# Revit family: Casement_34_D_Top_Hung_Standard
name_source: partatom
category: Windows
revit_build: Autodesk Revit 2014 (Build: 20130308_1515(x64)
units: mm (PartAtom-declared; Revit-internal decimal feet)

## types (12) — shared parameters
Aluminium Thickness = 1 mm  [stored 0.00328084 ft]
Bead SG Gap = 13 mm  [stored 0.0426509 ft]
Bottom Hung = No
Casement Dimension = 34 mm  [stored 0.111549 ft]
Custom Sash Height = 554 mm  [stored 1.81759 ft]
DG Extrusion Start = 7 mm  [stored 0.0229659 ft]
DG Gasket Finish = Double Glazing Gasket Material
DG Thickness Calc = 4 mm  [stored 0.0131234 ft]
Default Sill Height = 800 mm  [stored 2.62467 ft]
Depth Bead = 20 mm  [stored 0.0656168 ft]
Description = Window 34mm, Type D top hung
Frame Center Offset = 17 mm
Height Panel 1 = 540 mm  [stored 1.77165 ft]
Height Sash = 524 mm  [stored 1.71916 ft]
Height Sash Opening = 554 mm  [stored 1.81759 ft]
Limit Fixed Pane Height Max = 1800 mm  [stored 5.90551 ft]
Limit Fixed Pane Height Min = 200 mm  [stored 0.656168 ft]
Limit Sash Height Max = 900 mm  [stored 2.95276 ft]
Limit Sash Height Min = 300 mm  [stored 0.984252 ft]
Limit Sash Width Max = 1200 mm
Limit Sash Width Min = 300 mm  [stored 0.984252 ft]
Limit Window Height Max = 2430 mm
Limit Window Height Min = 830 mm  [stored 2.7231 ft]
Limit Window Width Max = 1246 mm  [stored 4.08793 ft]
Limit Window Width Min = 346 mm
Manufacturer = Crealco
Max System DG One Piece Thickness = 4 mm  [stored 0.0131234 ft]
Max System DG Unit Thickness = 20 mm  [stored 0.0656168 ft]
Model = Casement 34
Offset Bead SG Center Reversed = 17 mm
Offset Panel 3 Bead Top = 600 mm  [stored 1.9685 ft]
Offset Sash Left = 23 mm  [stored 0.0754593 ft]
Offset Sash Top = 23 mm  [stored 0.0754593 ft]
Offset Transom Top = 570 mm  [stored 1.87008 ft]
Offset Window Exterior = 17 mm
SG Gasket Thickness = 6 mm  [stored 0.019685 ft]
Sash Center Offset = 14 mm  [stored 0.0459318 ft]
Sash Overlap = 7 mm  [stored 0.0229659 ft]
Sash Spacing Inner = 8 mm  [stored 0.0262467 ft]
Top Hung = Yes
URL = http://www.crealco.co.za
Wall Closure = By host
Width Bead = 15 mm  [stored 0.0492126 ft]
Width Profile = 30 mm  [stored 0.0984252 ft]
zero-valued in all types: Window Exterior Offset

## per-type parameters (varying)
- 34-0609T-1000Pa: Area Pane Bottom=0.13 m²; Area Pane Top=0.23 m²; Clearvue Insulated LowE SHGC Value=0.43; Clearvue Insulated LowE U Value=3.94; Clearvue Insulated SHGC Value=0.471; Clearvue Insulated U Value=4.36; Clearvue SHGC Value=0.529; Clearvue U Value=6.18; Custom Windload=1000 mm  [stored 3.28084 ft]; Custom Window Height=890 mm  [stored 2.91995 ft]; Custom Window Width=590 mm  [stored 1.9357 ft]; Energy Advantage SHGC Value=0.475; Energy Advantage U Value=4.96; Height=890 mm  [stored 2.91995 ft]; Height Panel 3=260 mm; Intruderprufe LowE SHGC Value=0.446; Intruderprufe LowE U Value=4.84; Intruderprufe SHGC Value=0.499; Intruderprufe U Value=6.13; Length Transom=530 mm  [stored 1.73885 ft]; Max Pane Area=0.23 m²; Width=590 mm  [stored 1.9357 ft]; Width Panel 1=530 mm  [stored 1.73885 ft]; Width Panel 3=530 mm  [stored 1.73885 ft]; Width Sash=514 mm; Width Sash Opening=544 mm  [stored 1.78478 ft]; Windload Design=1000 mm  [stored 3.28084 ft]
- 34-0609T-1500Pa: Area Pane Bottom=0.13 m²; Area Pane Top=0.23 m²; Clearvue Insulated LowE SHGC Value=0.43; Clearvue Insulated LowE U Value=3.94; Clearvue Insulated SHGC Value=0.471; Clearvue Insulated U Value=4.36; Clearvue SHGC Value=0.529; Clearvue U Value=6.18; Custom Windload=1500 mm  [stored 4.92126 ft]; Custom Window Height=890 mm  [stored 2.91995 ft]; Custom Window Width=590 mm  [stored 1.9357 ft]; Energy Advantage SHGC Value=0.475; Energy Advantage U Value=4.96; Height=890 mm  [stored 2.91995 ft]; Height Panel 3=260 mm; Intruderprufe LowE SHGC Value=0.446; Intruderprufe LowE U Value=4.84; Intruderprufe SHGC Value=0.499; Intruderprufe U Value=6.13; Length Transom=530 mm  [stored 1.73885 ft]; Max Pane Area=0.23 m²; Width=590 mm  [stored 1.9357 ft]; Width Panel 1=530 mm  [stored 1.73885 ft]; Width Panel 3=530 mm  [stored 1.73885 ft]; Width Sash=514 mm; Width Sash Opening=544 mm  [stored 1.78478 ft]; Windload Design=1500 mm  [stored 4.92126 ft]
- 34-0609T-2000Pa: Area Pane Bottom=0.13 m²; Area Pane Top=0.23 m²; Clearvue Insulated LowE SHGC Value=0.43; Clearvue Insulated LowE U Value=3.94; Clearvue Insulated SHGC Value=0.471; Clearvue Insulated U Value=4.36; Clearvue SHGC Value=0.529; Clearvue U Value=6.18; Custom Windload=2000 mm; Custom Window Height=890 mm  [stored 2.91995 ft]; Custom Window Width=590 mm  [stored 1.9357 ft]; Energy Advantage SHGC Value=0.475; Energy Advantage U Value=4.96; Height=890 mm  [stored 2.91995 ft]; Height Panel 3=260 mm; Intruderprufe LowE SHGC Value=0.446; Intruderprufe LowE U Value=4.84; Intruderprufe SHGC Value=0.499; Intruderprufe U Value=6.13; Length Transom=530 mm  [stored 1.73885 ft]; Max Pane Area=0.23 m²; Width=590 mm  [stored 1.9357 ft]; Width Panel 1=530 mm  [stored 1.73885 ft]; Width Panel 3=530 mm  [stored 1.73885 ft]; Width Sash=514 mm; Width Sash Opening=544 mm  [stored 1.78478 ft]; Windload Design=2000 mm
- 34-0909T-1000Pa: Area Pane Bottom=0.21 m²; Area Pane Top=0.37 m²; Clearvue Insulated LowE SHGC Value=0.465; Clearvue Insulated LowE U Value=3.68; Clearvue Insulated SHGC Value=0.51; Clearvue Insulated U Value=4.15; Clearvue SHGC Value=0.574; Clearvue U Value=6.15; Custom Windload=1000 mm  [stored 3.28084 ft]; Custom Window Height=890 mm  [stored 2.91995 ft]; Custom Window Width=890 mm  [stored 2.91995 ft]; Energy Advantage SHGC Value=0.514; Energy Advantage U Value=4.79; Height=890 mm  [stored 2.91995 ft]; Height Panel 3=260 mm; Intruderprufe LowE SHGC Value=0.483; Intruderprufe LowE U Value=4.68; Intruderprufe SHGC Value=0.542; Intruderprufe U Value=6.1; Length Transom=830 mm  [stored 2.7231 ft]; Max Pane Area=0.37 m²; Width=890 mm  [stored 2.91995 ft]; Width Panel 1=830 mm  [stored 2.7231 ft]; Width Panel 3=830 mm  [stored 2.7231 ft]; Width Sash=814 mm  [stored 2.6706 ft]; Width Sash Opening=844 mm  [stored 2.76903 ft]; Windload Design=1000 mm  [stored 3.28084 ft]
- 34-0909T-1500Pa: Area Pane Bottom=0.21 m²; Area Pane Top=0.37 m²; Clearvue Insulated LowE SHGC Value=0.465; Clearvue Insulated LowE U Value=3.68; Clearvue Insulated SHGC Value=0.51; Clearvue Insulated U Value=4.15; Clearvue SHGC Value=0.574; Clearvue U Value=6.15; Custom Windload=1500 mm  [stored 4.92126 ft]; Custom Window Height=890 mm  [stored 2.91995 ft]; Custom Window Width=890 mm  [stored 2.91995 ft]; Energy Advantage SHGC Value=0.514; Energy Advantage U Value=4.79; Height=890 mm  [stored 2.91995 ft]; Height Panel 3=260 mm; Intruderprufe LowE SHGC Value=0.483; Intruderprufe LowE U Value=4.68; Intruderprufe SHGC Value=0.542; Intruderprufe U Value=6.1; Length Transom=830 mm  [stored 2.7231 ft]; Max Pane Area=0.37 m²; Width=890 mm  [stored 2.91995 ft]; Width Panel 1=830 mm  [stored 2.7231 ft]; Width Panel 3=830 mm  [stored 2.7231 ft]; Width Sash=814 mm  [stored 2.6706 ft]; Width Sash Opening=844 mm  [stored 2.76903 ft]; Windload Design=1500 mm  [stored 4.92126 ft]
- 34-0909T-2000Pa: Area Pane Bottom=0.21 m²; Area Pane Top=0.37 m²; Clearvue Insulated LowE SHGC Value=0.465; Clearvue Insulated LowE U Value=3.68; Clearvue Insulated SHGC Value=0.51; Clearvue Insulated U Value=4.15; Clearvue SHGC Value=0.574; Clearvue U Value=6.15; Custom Windload=2000 mm; Custom Window Height=890 mm  [stored 2.91995 ft]; Custom Window Width=890 mm  [stored 2.91995 ft]; Energy Advantage SHGC Value=0.514; Energy Advantage U Value=4.79; Height=890 mm  [stored 2.91995 ft]; Height Panel 3=260 mm; Intruderprufe LowE SHGC Value=0.483; Intruderprufe LowE U Value=4.68; Intruderprufe SHGC Value=0.542; Intruderprufe U Value=6.1; Length Transom=830 mm  [stored 2.7231 ft]; Max Pane Area=0.37 m²; Width=890 mm  [stored 2.91995 ft]; Width Panel 1=830 mm  [stored 2.7231 ft]; Width Panel 3=830 mm  [stored 2.7231 ft]; Width Sash=814 mm  [stored 2.6706 ft]; Width Sash Opening=844 mm  [stored 2.76903 ft]; Windload Design=2000 mm
- 34-0612T-1000Pa: Area Pane Bottom=0.29 m²; Area Pane Top=0.23 m²; Clearvue Insulated LowE SHGC Value=0.467; Clearvue Insulated LowE U Value=3.65; Clearvue Insulated SHGC Value=0.513; Clearvue Insulated U Value=4.12; Clearvue SHGC Value=0.576; Clearvue U Value=6.13; Custom Windload=1000 mm  [stored 3.28084 ft]; Custom Window Height=1190 mm  [stored 3.9042 ft]; Custom Window Width=590 mm  [stored 1.9357 ft]; Energy Advantage SHGC Value=0.516; Energy Advantage U Value=4.77; Height=1190 mm  [stored 3.9042 ft]; Height Panel 3=560 mm; Intruderprufe LowE SHGC Value=0.485; Intruderprufe LowE U Value=4.66; Intruderprufe SHGC Value=0.544; Intruderprufe U Value=6.06; Length Transom=530 mm  [stored 1.73885 ft]; Max Pane Area=0.29 m²; Width=590 mm  [stored 1.9357 ft]; Width Panel 1=530 mm  [stored 1.73885 ft]; Width Panel 3=530 mm  [stored 1.73885 ft]; Width Sash=514 mm; Width Sash Opening=544 mm  [stored 1.78478 ft]; Windload Design=1000 mm  [stored 3.28084 ft]
- 34-0612T-1500Pa: Area Pane Bottom=0.29 m²; Area Pane Top=0.23 m²; Clearvue Insulated LowE SHGC Value=0.467; Clearvue Insulated LowE U Value=3.65; Clearvue Insulated SHGC Value=0.513; Clearvue Insulated U Value=4.12; Clearvue SHGC Value=0.576; Clearvue U Value=6.13; Custom Windload=1500 mm  [stored 4.92126 ft]; Custom Window Height=1190 mm  [stored 3.9042 ft]; Custom Window Width=590 mm  [stored 1.9357 ft]; Energy Advantage SHGC Value=0.516; Energy Advantage U Value=4.77; Height=1190 mm  [stored 3.9042 ft]; Height Panel 3=560 mm; Intruderprufe LowE SHGC Value=0.485; Intruderprufe LowE U Value=4.66; Intruderprufe SHGC Value=0.544; Intruderprufe U Value=6.06; Length Transom=530 mm  [stored 1.73885 ft]; Max Pane Area=0.29 m²; Width=590 mm  [stored 1.9357 ft]; Width Panel 1=530 mm  [stored 1.73885 ft]; Width Panel 3=530 mm  [stored 1.73885 ft]; Width Sash=514 mm; Width Sash Opening=544 mm  [stored 1.78478 ft]; Windload Design=1500 mm  [stored 4.92126 ft]
- 34-0612T-2000Pa: Area Pane Bottom=0.29 m²; Area Pane Top=0.23 m²; Clearvue Insulated LowE SHGC Value=0.467; Clearvue Insulated LowE U Value=3.65; Clearvue Insulated SHGC Value=0.513; Clearvue Insulated U Value=4.12; Clearvue SHGC Value=0.576; Clearvue U Value=6.13; Custom Windload=2000 mm; Custom Window Height=1190 mm  [stored 3.9042 ft]; Custom Window Width=590 mm  [stored 1.9357 ft]; Energy Advantage SHGC Value=0.516; Energy Advantage U Value=4.77; Height=1190 mm  [stored 3.9042 ft]; Height Panel 3=560 mm; Intruderprufe LowE SHGC Value=0.485; Intruderprufe LowE U Value=4.66; Intruderprufe SHGC Value=0.544; Intruderprufe U Value=6.06; Length Transom=530 mm  [stored 1.73885 ft]; Max Pane Area=0.29 m²; Width=590 mm  [stored 1.9357 ft]; Width Panel 1=530 mm  [stored 1.73885 ft]; Width Panel 3=530 mm  [stored 1.73885 ft]; Width Sash=514 mm; Width Sash Opening=544 mm  [stored 1.78478 ft]; Windload Design=2000 mm
- 34-0912T-1000Pa: Area Pane Bottom=0.45 m²; Area Pane Top=0.37 m²; Clearvue Insulated LowE SHGC Value=0.502; Clearvue Insulated LowE U Value=3.38; Clearvue Insulated SHGC Value=0.552; Clearvue Insulated U Value=3.91; Clearvue SHGC Value=0.621; Clearvue U Value=6.1; Custom Windload=1000 mm  [stored 3.28084 ft]; Custom Window Height=1190 mm  [stored 3.9042 ft]; Custom Window Width=890 mm  [stored 2.91995 ft]; Energy Advantage SHGC Value=0.556; Energy Advantage U Value=4.6; Height=1190 mm  [stored 3.9042 ft]; Height Panel 3=560 mm; Intruderprufe LowE SHGC Value=0.521; Intruderprufe LowE U Value=4.49; Intruderprufe SHGC Value=0.587; Intruderprufe U Value=6.02; Length Transom=830 mm  [stored 2.7231 ft]; Max Pane Area=0.45 m²; Width=890 mm  [stored 2.91995 ft]; Width Panel 1=830 mm  [stored 2.7231 ft]; Width Panel 3=830 mm  [stored 2.7231 ft]; Width Sash=814 mm  [stored 2.6706 ft]; Width Sash Opening=844 mm  [stored 2.76903 ft]; Windload Design=1000 mm  [stored 3.28084 ft]
- 34-0912T-1500Pa: Area Pane Bottom=0.45 m²; Area Pane Top=0.37 m²; Clearvue Insulated LowE SHGC Value=0.502; Clearvue Insulated LowE U Value=3.38; Clearvue Insulated SHGC Value=0.552; Clearvue Insulated U Value=3.91; Clearvue SHGC Value=0.621; Clearvue U Value=6.1; Custom Windload=1500 mm  [stored 4.92126 ft]; Custom Window Height=1190 mm  [stored 3.9042 ft]; Custom Window Width=890 mm  [stored 2.91995 ft]; Energy Advantage SHGC Value=0.556; Energy Advantage U Value=4.6; Height=1190 mm  [stored 3.9042 ft]; Height Panel 3=560 mm; Intruderprufe LowE SHGC Value=0.521; Intruderprufe LowE U Value=4.49; Intruderprufe SHGC Value=0.587; Intruderprufe U Value=6.02; Length Transom=830 mm  [stored 2.7231 ft]; Max Pane Area=0.45 m²; Width=890 mm  [stored 2.91995 ft]; Width Panel 1=830 mm  [stored 2.7231 ft]; Width Panel 3=830 mm  [stored 2.7231 ft]; Width Sash=814 mm  [stored 2.6706 ft]; Width Sash Opening=844 mm  [stored 2.76903 ft]; Windload Design=1500 mm  [stored 4.92126 ft]
- 34-0912T-2000Pa: Area Pane Bottom=0.45 m²; Area Pane Top=0.37 m²; Clearvue Insulated LowE SHGC Value=0.502; Clearvue Insulated LowE U Value=3.38; Clearvue Insulated SHGC Value=0.552; Clearvue Insulated U Value=3.91; Clearvue SHGC Value=0.621; Clearvue U Value=6.1; Custom Windload=2000 mm; Custom Window Height=1190 mm  [stored 3.9042 ft]; Custom Window Width=890 mm  [stored 2.91995 ft]; Energy Advantage SHGC Value=0.556; Energy Advantage U Value=4.6; Height=1190 mm  [stored 3.9042 ft]; Height Panel 3=560 mm; Intruderprufe LowE SHGC Value=0.521; Intruderprufe LowE U Value=4.49; Intruderprufe SHGC Value=0.587; Intruderprufe U Value=6.02; Length Transom=830 mm  [stored 2.7231 ft]; Max Pane Area=0.45 m²; Width=890 mm  [stored 2.91995 ft]; Width Panel 1=830 mm  [stored 2.7231 ft]; Width Panel 3=830 mm  [stored 2.7231 ft]; Width Sash=814 mm  [stored 2.6706 ft]; Width Sash Opening=844 mm  [stored 2.76903 ft]; Windload Design=2000 mm

note: [stored X ft] marks values corroborated as IEEE doubles in the binary element streams (Revit-internal decimal feet)

## geometry (parser evidence)
native form markers: Blend x4, Extrusion x1, Sweep x24
no freeform markers — native parametric forms only
